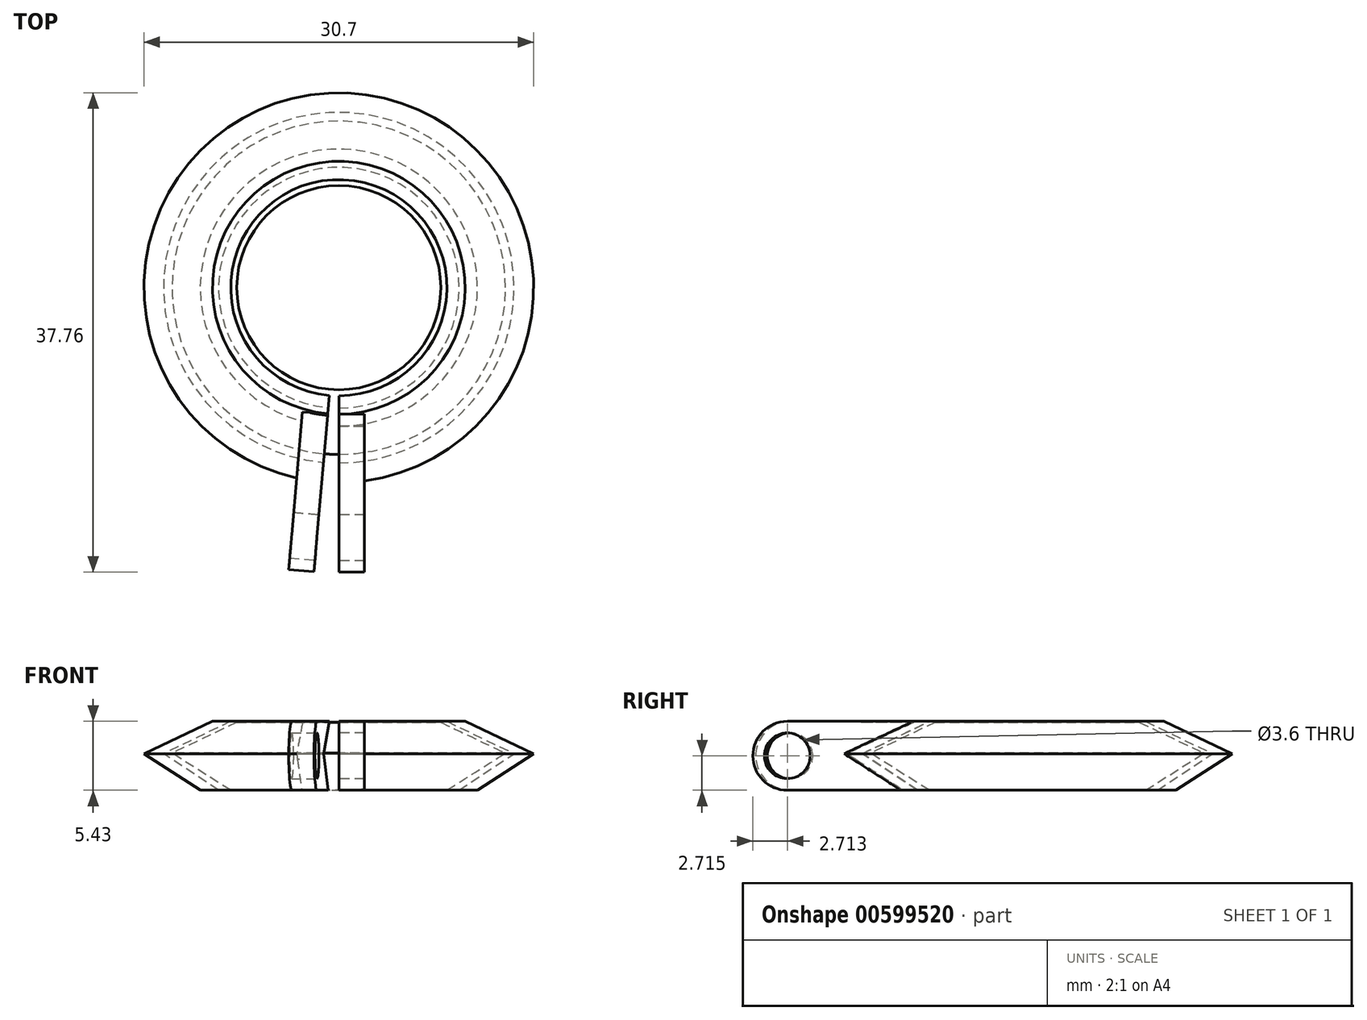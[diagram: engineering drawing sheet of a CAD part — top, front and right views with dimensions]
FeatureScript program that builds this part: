
annotation { "Feature Type Name" : "Feature", "Feature Type Description" : "" }
export const myFeature = defineFeature(function(context is Context, id is Id, definition is map)
    precondition{}
    {
        {
            var Q0;
            Q0=qCreatedBy(makeId("Front.planeOp"),FACE);
            var sketch = newSketch(context, id + "F0", { "sketchPlane" : qUnion([Q0])});
            skLineSegment(sketch, "E0", {"start": v(0, 0) * mm, "end": v(-8.53, 0) * mm});
            skLineSegment(sketch, "E1", {"start": v(-8.53, 0) * mm, "end": v(-13.14, 2.92) * mm});
            skLineSegment(sketch, "E2", {"start": v(-13.14, 2.92) * mm, "end": v(-8.04, 5.35) * mm});
            skLineSegment(sketch, "E3", {"start": v(-8.04, 5.35) * mm, "end": v(0, 5.35) * mm});
            skLineSegment(sketch, "E4", {"start": v(0, 5.35) * mm, "end": v(0, 0) * mm});
            skSolve(sketch);
        }
        {
            var Q0;
            Q0 = qSketchRegion(id + "F0", true);
            var Q1;
            Q1=sQuery(id+"F0.wireOp",EDGE,"E4");
            revolve(context, id + "F1", {"entities" : qUnion([Q0]), "axis" : qUnion([Q1]), "revolveType" : RevolveType.FULL});
        }
        {
            var Q0;
            Q0=qCreatedBy(makeId("Right.planeOp"),FACE);
            var sketch = newSketch(context, id + "F2", { "sketchPlane" : qUnion([Q0])});
            skLineSegment(sketch, "E5", {"start": v(-9.48, 0) * mm, "end": v(-13.81, 2.88) * mm});
            skLineSegment(sketch, "E6", {"start": v(-13.81, 2.88) * mm, "end": v(-8.52, 5.43) * mm});
            skLineSegment(sketch, "E7", {"start": v(-8.52, 5.43) * mm, "end": v(-9.96, 5.43) * mm});
            skLineSegment(sketch, "E8", {"start": v(-9.96, 5.43) * mm, "end": v(-15.35, 2.88) * mm});
            skLineSegment(sketch, "E9", {"start": v(-15.35, 2.88) * mm, "end": v(-10.92, 0) * mm});
            skLineSegment(sketch, "E10", {"start": v(-10.92, 0) * mm, "end": v(-9.48, 0) * mm});
            skSolve(sketch);
        }
        {
            var Q0;
            Q0=qCreatedBy(makeId("Right.planeOp"),FACE);
            var sketch = newSketch(context, id + "F3", { "sketchPlane" : qUnion([Q0])});
            skLineSegment(sketch, "E11", {"start": v(0, 0) * mm, "end": v(0, 6.9) * mm, "construction": true});
            skSolve(sketch);
        }
        {
            var Q0;
            Q0 = qSketchRegion(id + "F2", true);
            var Q1;
            Q1=sQuery(id+"F3.wireOp",EDGE,"E11");
            revolve(context, id + "F4", {"entities" : qUnion([Q0]), "axis" : qUnion([Q1]), "revolveType" : RevolveType.ONE_DIRECTION, "angle" : 355 * degree});
        }
        {
            var Q0;
            Q0=makeQuery(id+"F4.opRevolve","CAP_FACE",FACE,{"disambiguationData":[OSD([sQuery(id+"F2.wireOp",EDGE,"E5"),sQuery(id+"F2.wireOp",EDGE,"E6"),sQuery(id+"F2.wireOp",EDGE,"E7"),sQuery(id+"F2.wireOp",EDGE,"E8"),sQuery(id+"F2.wireOp",EDGE,"E9"),sQuery(id+"F2.wireOp",EDGE,"E10")])],"isStart":true});
            var sketch = newSketch(context, id + "F5", { "sketchPlane" : qUnion([Q0])});
            skLineSegment(sketch, "E12", {"start": v(9.96, 5.43) * mm, "end": v(19.7, 5.43) * mm});
            skLineSegment(sketch, "E13", {"start": v(19.7, 5.43) * mm, "end": v(19.7, 0) * mm});
            skLineSegment(sketch, "E14", {"start": v(19.7, 0) * mm, "end": v(10.92, 0) * mm});
            skCircle(sketch, "E15", {"center": v(19.7, 2.72) * mm, "radius": 2.72 * mm});
            skCircle(sketch, "E16", {"center": v(19.7, 2.72) * mm, "radius": 1.8 * mm});
            skLineSegment(sketch, "E17", {"start": v(9.96, 5.43) * mm, "end": v(9.96, 5.14) * mm});
            skLineSegment(sketch, "E18", {"start": v(9.96, 5.14) * mm, "end": v(17.17, 1.73) * mm});
            skLineSegment(sketch, "E19", {"start": v(10.92, 0) * mm, "end": v(10.92, 0.24) * mm});
            skLineSegment(sketch, "E20", {"start": v(10.92, 0.24) * mm, "end": v(18.06, 4.88) * mm});
            skSolve(sketch);
        }
        {
            var Q0;
            Q0 = qSketchRegion(id + "F5", true);
            extrude(context, id + "F6", {"entities" : qUnion([Q0]), "operationType" : NewBodyOperationType.ADD, "oppositeDirection" : true, "depth" : 2 * mm, "offsetDistance" : 25 * mm});
        }
        {
            var Q0;
            Q0=makeQuery(id+"F4.opRevolve","CAP_FACE",FACE,{"disambiguationData":[OSD([sQuery(id+"F2.wireOp",EDGE,"E5"),sQuery(id+"F2.wireOp",EDGE,"E6"),sQuery(id+"F2.wireOp",EDGE,"E7"),sQuery(id+"F2.wireOp",EDGE,"E8"),sQuery(id+"F2.wireOp",EDGE,"E9"),sQuery(id+"F2.wireOp",EDGE,"E10")])],"isStart":false});
            cPlane(context, id + "F7", {"entities" : qUnion([Q0]), "cplaneType" : CPlaneType.OFFSET, "offset" : 0 * mm, "width" : 150 * mm, "height" : 150 * mm});
        }
        {
            var Q0;
            Q0=qCreatedBy(id+"F7.planeOp",FACE);
            var sketch = newSketch(context, id + "F8", { "sketchPlane" : qUnion([Q0])});
            skLineSegment(sketch, "E21", {"start": v(-10, 0) * mm, "end": v(-19.74, 0) * mm});
            skLineSegment(sketch, "E22", {"start": v(-19.74, 0) * mm, "end": v(-19.74, 5.43) * mm});
            skLineSegment(sketch, "E23", {"start": v(-19.74, 5.43) * mm, "end": v(-10, 5.37) * mm});
            skCircle(sketch, "E24", {"center": v(-19.74, 2.72) * mm, "radius": 2.72 * mm});
            skCircle(sketch, "E25", {"center": v(-19.74, 2.72) * mm, "radius": 1.8 * mm});
            skLineSegment(sketch, "E26", {"start": v(-10, 0) * mm, "end": v(-10, 0.29) * mm});
            skLineSegment(sketch, "E27", {"start": v(-10, 0.29) * mm, "end": v(-17.21, 3.7) * mm});
            skLineSegment(sketch, "E28", {"start": v(-10, 5.37) * mm, "end": v(-10, 4.96) * mm});
            skLineSegment(sketch, "E29", {"start": v(-10, 4.96) * mm, "end": v(-18.1, 0.55) * mm});
            skSolve(sketch);
        }
        {
            var Q0;
            Q0 = qSketchRegion(id + "F8", true);
            extrude(context, id + "F9", {"entities" : qUnion([Q0]), "operationType" : NewBodyOperationType.ADD, "oppositeDirection" : true, "depth" : 2 * mm, "offsetDistance" : 25 * mm});
        }
    });
